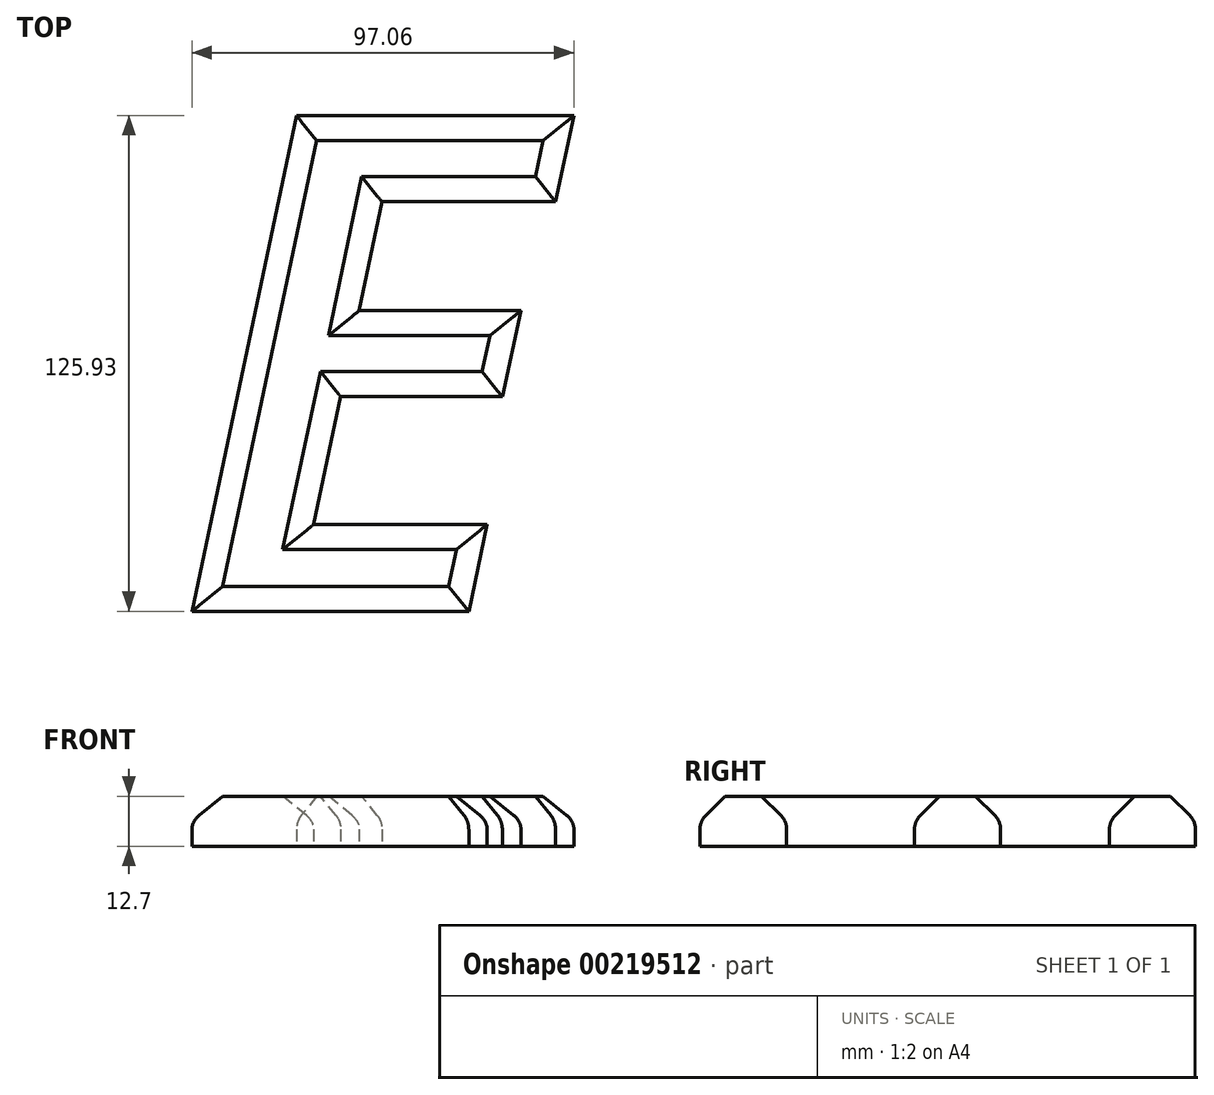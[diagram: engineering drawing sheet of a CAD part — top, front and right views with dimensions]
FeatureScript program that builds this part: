
annotation { "Feature Type Name" : "Feature", "Feature Type Description" : "" }
export const myFeature = defineFeature(function(context is Context, id is Id, definition is map)
    precondition{}
    {
        {
            var Q0;
            Q0=qCreatedBy(makeId("Top.planeOp"),FACE);
            var sketch = newSketch(context, id + "F0", { "sketchPlane" : qUnion([Q0])});
            skText(sketch, "E0", { "text": "E", "fontName": "OpenSans-BoldItalic.ttf"});
            const initialGuessF0  = {"E0": [-0.05656, -0.06469, 1, 0, 0.127]};
            skSetInitialGuess(sketch, initialGuessF0);
            skSolve(sketch);
        }
        {
            var Q0;
            Q0=makeQuery(id+"F0.imprint","IMPRINT",FACE,{"disambiguationData":[TD([[makeQuery(id+"F0.imprint","IMPRINT",EDGE,{"derivedFrom":sQuery(id+"F0.wireOp",EDGE,"E0.sketch_text.stroke-0")}),-1.0]])]});
            extrude(context, id + "F1", {"entities" : qUnion([Q0]), "depth" : 12.7 * mm});
        }
        {
            var Q0;
            Q0=makeQuery(id+"F1.opExtrude","CAP_FACE",FACE,{"disambiguationData":[OSD([sQuery(id+"F0.wireOp",EDGE,"E0.sketch_text.stroke-0"),sQuery(id+"F0.wireOp",EDGE,"E0.sketch_text.stroke-1"),sQuery(id+"F0.wireOp",EDGE,"E0.sketch_text.stroke-2"),sQuery(id+"F0.wireOp",EDGE,"E0.sketch_text.stroke-3"),sQuery(id+"F0.wireOp",EDGE,"E0.sketch_text.stroke-4"),sQuery(id+"F0.wireOp",EDGE,"E0.sketch_text.stroke-5"),sQuery(id+"F0.wireOp",EDGE,"E0.sketch_text.stroke-6"),sQuery(id+"F0.wireOp",EDGE,"E0.sketch_text.stroke-7"),sQuery(id+"F0.wireOp",EDGE,"E0.sketch_text.stroke-8"),sQuery(id+"F0.wireOp",EDGE,"E0.sketch_text.stroke-9"),sQuery(id+"F0.wireOp",EDGE,"E0.sketch_text.stroke-10"),sQuery(id+"F0.wireOp",EDGE,"E0.sketch_text.stroke-11")])],"isStart":false});
            chamfer(context, id + "F2", {"entities" : qUnion([Q0]), "width" : 6.35 * mm, "tangentPropagation" : true});
        }
        {
            var Q0;
            {var subQ0=sQuery(id+"F0.wireOp",EDGE,"E0.sketch_text.stroke-2");Q0=makeQuery(id+"F2.opChamfer","BLEND_EDGE",EDGE,{"blendedFrom":[makeQuery(id+"F1.opExtrude","CAP_EDGE",EDGE,{"disambiguationData":[OSD([subQ0])],"isStart":false}),makeQuery(id+"F1.opExtrude","SWEPT_FACE",FACE,{"disambiguationData":[OSD([subQ0])]})],"blendedInto":[makeQuery(id+"F1.opExtrude","SWEPT_FACE",FACE,{"disambiguationData":[OSD([subQ0])]})]});}
            var Q1;
            {var subQ0=sQuery(id+"F0.wireOp",EDGE,"E0.sketch_text.stroke-1");Q1=makeQuery(id+"F2.opChamfer","BLEND_EDGE",EDGE,{"blendedFrom":[makeQuery(id+"F1.opExtrude","CAP_EDGE",EDGE,{"disambiguationData":[OSD([subQ0])],"isStart":false}),makeQuery(id+"F1.opExtrude","SWEPT_FACE",FACE,{"disambiguationData":[OSD([subQ0])]})],"blendedInto":[makeQuery(id+"F1.opExtrude","SWEPT_FACE",FACE,{"disambiguationData":[OSD([subQ0])]})]});}
            var Q2;
            {var subQ0=sQuery(id+"F0.wireOp",EDGE,"E0.sketch_text.stroke-3");Q2=makeQuery(id+"F2.opChamfer","BLEND_EDGE",EDGE,{"blendedFrom":[makeQuery(id+"F1.opExtrude","CAP_EDGE",EDGE,{"disambiguationData":[OSD([subQ0])],"isStart":false}),makeQuery(id+"F1.opExtrude","SWEPT_FACE",FACE,{"disambiguationData":[OSD([subQ0])]})],"blendedInto":[makeQuery(id+"F1.opExtrude","SWEPT_FACE",FACE,{"disambiguationData":[OSD([subQ0])]})]});}
            var Q3;
            {var subQ0=sQuery(id+"F0.wireOp",EDGE,"E0.sketch_text.stroke-4");Q3=makeQuery(id+"F2.opChamfer","BLEND_EDGE",EDGE,{"blendedFrom":[makeQuery(id+"F1.opExtrude","CAP_EDGE",EDGE,{"disambiguationData":[OSD([subQ0])],"isStart":false}),makeQuery(id+"F1.opExtrude","SWEPT_FACE",FACE,{"disambiguationData":[OSD([subQ0])]})],"blendedInto":[makeQuery(id+"F1.opExtrude","SWEPT_FACE",FACE,{"disambiguationData":[OSD([subQ0])]})]});}
            var Q4;
            {var subQ0=sQuery(id+"F0.wireOp",EDGE,"E0.sketch_text.stroke-5");Q4=makeQuery(id+"F2.opChamfer","BLEND_EDGE",EDGE,{"blendedFrom":[makeQuery(id+"F1.opExtrude","CAP_EDGE",EDGE,{"disambiguationData":[OSD([subQ0])],"isStart":false}),makeQuery(id+"F1.opExtrude","SWEPT_FACE",FACE,{"disambiguationData":[OSD([subQ0])]})],"blendedInto":[makeQuery(id+"F1.opExtrude","SWEPT_FACE",FACE,{"disambiguationData":[OSD([subQ0])]})]});}
            var Q5;
            {var subQ0=sQuery(id+"F0.wireOp",EDGE,"E0.sketch_text.stroke-6");Q5=makeQuery(id+"F2.opChamfer","BLEND_EDGE",EDGE,{"blendedFrom":[makeQuery(id+"F1.opExtrude","CAP_EDGE",EDGE,{"disambiguationData":[OSD([subQ0])],"isStart":false}),makeQuery(id+"F1.opExtrude","SWEPT_FACE",FACE,{"disambiguationData":[OSD([subQ0])]})],"blendedInto":[makeQuery(id+"F1.opExtrude","SWEPT_FACE",FACE,{"disambiguationData":[OSD([subQ0])]})]});}
            var Q6;
            {var subQ0=sQuery(id+"F0.wireOp",EDGE,"E0.sketch_text.stroke-7");Q6=makeQuery(id+"F2.opChamfer","BLEND_EDGE",EDGE,{"blendedFrom":[makeQuery(id+"F1.opExtrude","CAP_EDGE",EDGE,{"disambiguationData":[OSD([subQ0])],"isStart":false}),makeQuery(id+"F1.opExtrude","SWEPT_FACE",FACE,{"disambiguationData":[OSD([subQ0])]})],"blendedInto":[makeQuery(id+"F1.opExtrude","SWEPT_FACE",FACE,{"disambiguationData":[OSD([subQ0])]})]});}
            var Q7;
            {var subQ0=sQuery(id+"F0.wireOp",EDGE,"E0.sketch_text.stroke-8");Q7=makeQuery(id+"F2.opChamfer","BLEND_EDGE",EDGE,{"blendedFrom":[makeQuery(id+"F1.opExtrude","CAP_EDGE",EDGE,{"disambiguationData":[OSD([subQ0])],"isStart":false}),makeQuery(id+"F1.opExtrude","SWEPT_FACE",FACE,{"disambiguationData":[OSD([subQ0])]})],"blendedInto":[makeQuery(id+"F1.opExtrude","SWEPT_FACE",FACE,{"disambiguationData":[OSD([subQ0])]})]});}
            var Q8;
            {var subQ0=sQuery(id+"F0.wireOp",EDGE,"E0.sketch_text.stroke-9");Q8=makeQuery(id+"F2.opChamfer","BLEND_EDGE",EDGE,{"blendedFrom":[makeQuery(id+"F1.opExtrude","CAP_EDGE",EDGE,{"disambiguationData":[OSD([subQ0])],"isStart":false}),makeQuery(id+"F1.opExtrude","SWEPT_FACE",FACE,{"disambiguationData":[OSD([subQ0])]})],"blendedInto":[makeQuery(id+"F1.opExtrude","SWEPT_FACE",FACE,{"disambiguationData":[OSD([subQ0])]})]});}
            var Q9;
            {var subQ0=sQuery(id+"F0.wireOp",EDGE,"E0.sketch_text.stroke-10");Q9=makeQuery(id+"F2.opChamfer","BLEND_EDGE",EDGE,{"blendedFrom":[makeQuery(id+"F1.opExtrude","CAP_EDGE",EDGE,{"disambiguationData":[OSD([subQ0])],"isStart":false}),makeQuery(id+"F1.opExtrude","SWEPT_FACE",FACE,{"disambiguationData":[OSD([subQ0])]})],"blendedInto":[makeQuery(id+"F1.opExtrude","SWEPT_FACE",FACE,{"disambiguationData":[OSD([subQ0])]})]});}
            var Q10;
            {var subQ0=sQuery(id+"F0.wireOp",EDGE,"E0.sketch_text.stroke-11");Q10=makeQuery(id+"F2.opChamfer","BLEND_EDGE",EDGE,{"blendedFrom":[makeQuery(id+"F1.opExtrude","CAP_EDGE",EDGE,{"disambiguationData":[OSD([subQ0])],"isStart":false}),makeQuery(id+"F1.opExtrude","SWEPT_FACE",FACE,{"disambiguationData":[OSD([subQ0])]})],"blendedInto":[makeQuery(id+"F1.opExtrude","SWEPT_FACE",FACE,{"disambiguationData":[OSD([subQ0])]})]});}
            var Q11;
            {var subQ0=sQuery(id+"F0.wireOp",EDGE,"E0.sketch_text.stroke-0");Q11=makeQuery(id+"F2.opChamfer","BLEND_EDGE",EDGE,{"blendedFrom":[makeQuery(id+"F1.opExtrude","CAP_EDGE",EDGE,{"disambiguationData":[OSD([subQ0])],"isStart":false}),makeQuery(id+"F1.opExtrude","SWEPT_FACE",FACE,{"disambiguationData":[OSD([subQ0])]})],"blendedInto":[makeQuery(id+"F1.opExtrude","SWEPT_FACE",FACE,{"disambiguationData":[OSD([subQ0])]})]});}
            fillet(context, id + "F3", {"entities" : qUnion([Q0, Q1, Q2, Q3, Q4, Q5, Q6, Q7, Q8, Q9, Q10, Q11]), "radius" : 5.08 * mm, "tangentPropagation" : true, "allowEdgeOverflow" : false});
        }
    });
